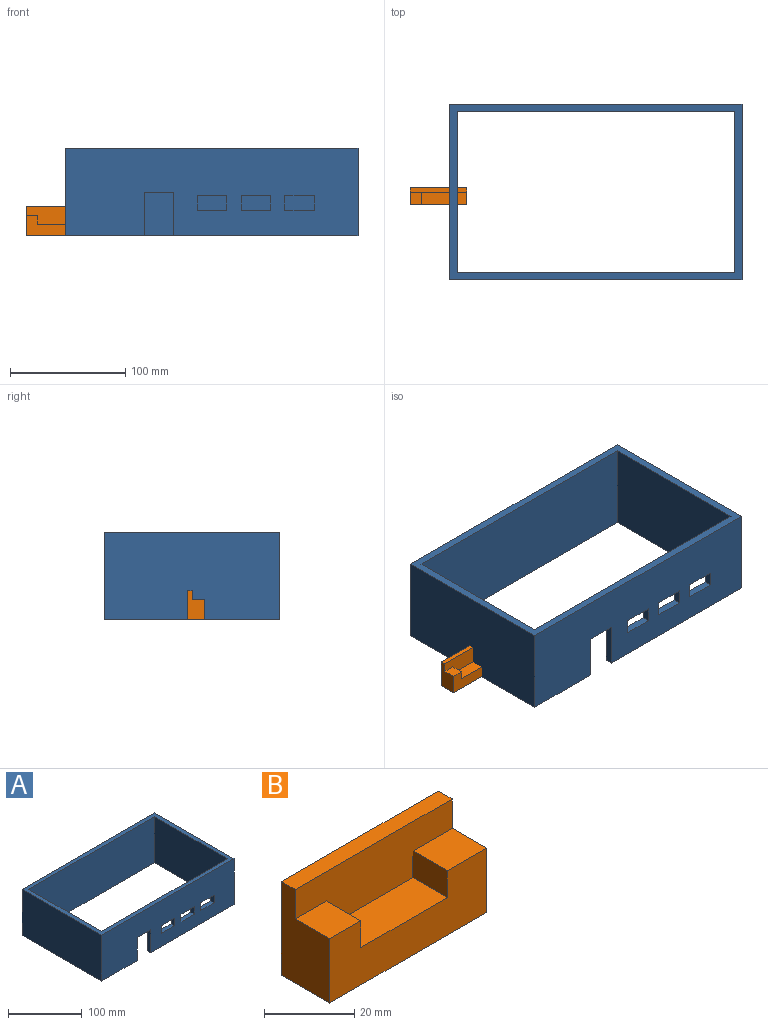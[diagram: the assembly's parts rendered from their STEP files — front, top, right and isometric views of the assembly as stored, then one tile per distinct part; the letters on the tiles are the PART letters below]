
ASSEMBLY  parts=2 mates=1
PART A: 25 faces, bbox 254x152.4x76.2 mm
  f0: plane 254x76.2mm, normal (0,-1,0), area 17419.3mm2, adj f4,f5,f8,f9,f10,f11,f12,f13
  f1: plane 241.3x76.2mm, normal (0,-1,0), area 18387.1mm2, adj f2,f7,f8,f9
  f2: plane 139.7x76.2mm, normal (-1,0,0), area 10645.1mm2, adj f1,f3,f8,f9
  f3: plane 241.3x76.2mm, normal (0,1,0), area 16451.6mm2, adj f2,f7,f8,f9,f10,f11,f12,f13
  f4: plane 152.4x76.2mm, normal (-1,0,0), area 11612.9mm2, adj f0,f6,f8,f9
  f5: plane 152.4x76.2mm, normal (1,0,0), area 11612.9mm2, adj f0,f6,f8,f9
  f6: plane 254x76.2mm, normal (0,1,0), area 19354.8mm2, adj f4,f5,f8,f9
  f7: plane 139.7x76.2mm, normal (1,0,0), area 10645.1mm2, adj f1,f3,f8,f9
  f8: plane 254x152.4mm, normal (0,0,1), area 5000mm2, adj f0,f1,f2,f3,f4,f5,f6,f7
  f9: plane 254x152.4mm, normal (0,0,-1), area 4838.7mm2, adj f0,f1,f2,f3,f4,f5,f6,f7
  f10: plane 38.1x6.35mm, normal (-1,0,0), area 241.9mm2, adj f0,f3,f9,f11
  f11: plane 25.4x6.35mm, normal (0,0,-1), area 161.3mm2, adj f0,f3,f10,f12
  f12: plane 38.1x6.35mm, normal (1,0,0), area 241.9mm2, adj f0,f3,f9,f11
  f13: plane 12.7x6.35mm, normal (1,0,0), area 80.6mm2, adj f0,f3,f14,f16
  f14: plane 25.4x6.35mm, normal (0,0,1), area 161.3mm2, adj f0,f3,f13,f15
  f15: plane 12.7x6.35mm, normal (-1,0,0), area 80.6mm2, adj f0,f3,f14,f16
  f16: plane 25.4x6.35mm, normal (0,0,-1), area 161.3mm2, adj f0,f3,f13,f15
  f17: plane 12.7x6.35mm, normal (1,0,0), area 80.6mm2, adj f0,f3,f18,f20
  f18: plane 25.4x6.35mm, normal (0,0,1), area 161.3mm2, adj f0,f3,f17,f19
  f19: plane 12.7x6.35mm, normal (-1,0,0), area 80.6mm2, adj f0,f3,f18,f20
  f20: plane 25.4x6.35mm, normal (0,0,-1), area 161.3mm2, adj f0,f3,f17,f19
  f21: plane 12.7x6.35mm, normal (1,0,0), area 80.6mm2, adj f0,f3,f22,f24
  f22: plane 25.4x6.35mm, normal (0,0,1), area 161.3mm2, adj f0,f3,f21,f23
  f23: plane 12.7x6.35mm, normal (-1,0,0), area 80.6mm2, adj f0,f3,f22,f24
  f24: plane 25.4x6.35mm, normal (0,0,-1), area 161.3mm2, adj f0,f3,f21,f23
PART B: 12 faces, bbox 49.2x15.1x25.4 mm
  f0: plane 25.4x15.15mm, normal (1,0,0), area 298.8mm2, adj f1,f3,f4,f5,f8,f10
  f1: plane 49.23x4.34mm, normal (0,0,1), area 213.6mm2, adj f0,f2,f4,f8
  f2: plane 25.4x15.15mm, normal (-1,0,0), area 298.8mm2, adj f1,f3,f4,f5,f8,f11
  f3: plane 49.23x17.45mm, normal (0,-1,0), area 660.9mm2, adj f0,f2,f5,f6,f7,f9,f10,f11
  f4: plane 49.23x25.4mm, normal (0,1,0), area 1250.4mm2, adj f0,f1,f2,f5
  f5: plane 49.23x15.15mm, normal (0,0,-1), area 745.7mm2, adj f0,f2,f3,f4
  f6: plane 10.81x7.29mm, normal (1,0,0), area 78.8mm2, adj f3,f8,f9,f11
  f7: plane 10.81x7.29mm, normal (-1,0,0), area 78.8mm2, adj f3,f8,f9,f10
  f8: plane 49.23x15.24mm, normal (0,-1,0), area 589.5mm2, adj f0,f1,f2,f6,f7,f9,f10,f11
  f9: plane 27.19x10.81mm, normal (0,0,1), area 293.9mm2, adj f3,f6,f7,f8
  f10: plane 12.29x10.81mm, normal (0,0,1), area 132.8mm2, adj f0,f3,f7,f8
  f11: plane 10.81x9.75mm, normal (0,0,1), area 105.4mm2, adj f2,f3,f6,f8
PLACE A t=(77.66,48.99,54.33)mm
PLACE B t=(13.96,-8.14,54.33)mm
MATE planar B.f5 <-> A.f9  axis (0,0,-1) through (-59.25,45.51,54.33)mm
